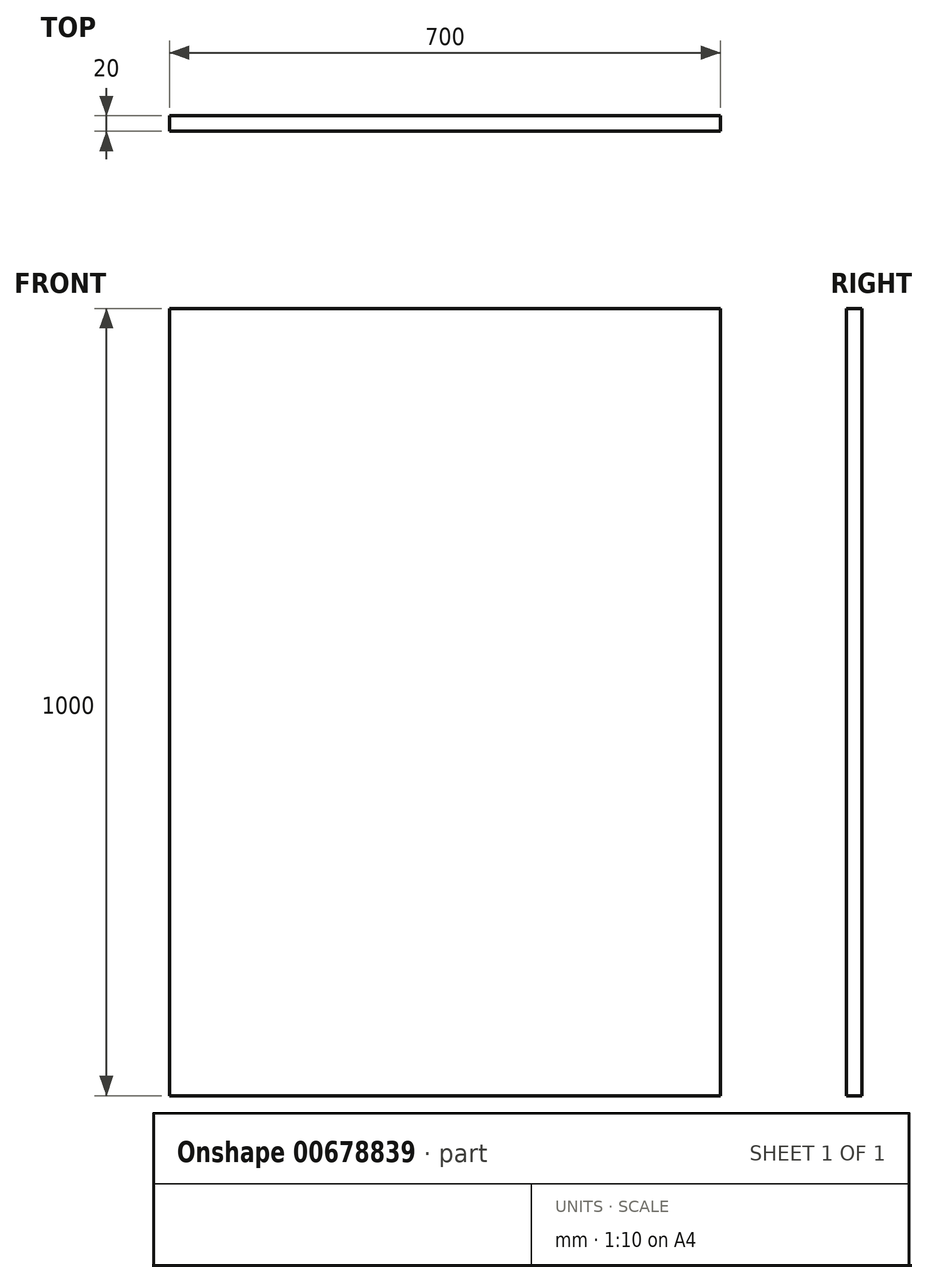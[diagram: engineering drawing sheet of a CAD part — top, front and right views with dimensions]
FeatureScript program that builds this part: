
annotation { "Feature Type Name" : "Feature", "Feature Type Description" : "" }
export const myFeature = defineFeature(function(context is Context, id is Id, definition is map)
    precondition{}
    {
        {
            var Q0;
            Q0=qCreatedBy(makeId("Front.planeOp"),FACE);
            var sketch = newSketch(context, id + "F0", { "sketchPlane" : qUnion([Q0])});
            skLineSegment(sketch, "E0.bottom", {"start": v(-350, 500) * mm, "end": v(350, 500) * mm});
            skLineSegment(sketch, "E0.top", {"start": v(-350, -500) * mm, "end": v(350, -500) * mm});
            skLineSegment(sketch, "E0.left", {"start": v(-350, 500) * mm, "end": v(-350, -500) * mm});
            skLineSegment(sketch, "E0.right", {"start": v(350, 500) * mm, "end": v(350, -500) * mm});
            skPoint(sketch, "E0.middle", {"position": v(0, 0) * mm});
            skSolve(sketch);
        }
        {
            var Q0;
            Q0 = qSketchRegion(id + "F0", true);
            extrude(context, id + "F1", {"entities" : qUnion([Q0]), "depth" : 20 * mm, "offsetDistance" : 25 * mm});
        }
    });
